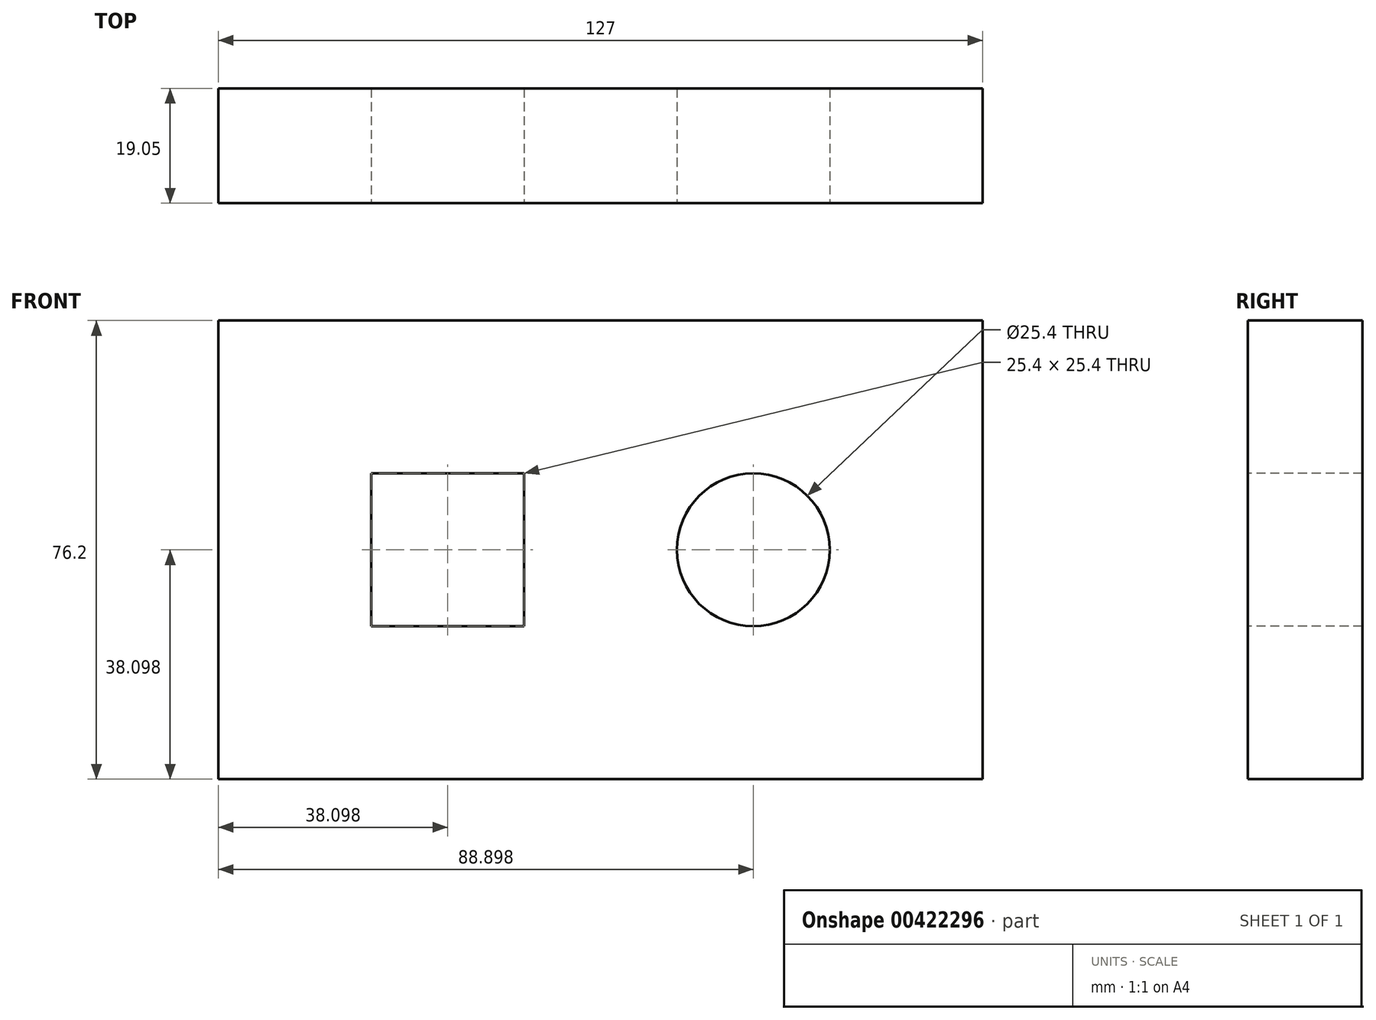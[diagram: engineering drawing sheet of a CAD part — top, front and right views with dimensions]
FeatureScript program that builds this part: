
annotation { "Feature Type Name" : "Feature", "Feature Type Description" : "" }
export const myFeature = defineFeature(function(context is Context, id is Id, definition is map)
    precondition{}
    {
        {
            var Q0;
            Q0=qCreatedBy(makeId("Front.planeOp"),FACE);
            var sketch = newSketch(context, id + "F0", { "sketchPlane" : qUnion([Q0])});
            skLineSegment(sketch, "E0.bottom", {"start": v(-64.45, 53.6) * mm, "end": v(62.55, 53.6) * mm});
            skLineSegment(sketch, "E0.top", {"start": v(-64.45, -22.6) * mm, "end": v(62.55, -22.6) * mm});
            skLineSegment(sketch, "E0.left", {"start": v(-64.45, 53.6) * mm, "end": v(-64.45, -22.6) * mm});
            skLineSegment(sketch, "E0.right", {"start": v(62.55, 53.6) * mm, "end": v(62.55, -22.6) * mm});
            skSolve(sketch);
        }
        {
            var Q0;
            Q0 = qSketchRegion(id + "F0", true);
            extrude(context, id + "F1", {"entities" : qUnion([Q0]), "depth" : 19.05 * mm});
        }
        {
            var Q0;
            Q0=makeQuery(id+"F1.opExtrude","CAP_FACE",FACE,{"disambiguationData":[OSD([sQuery(id+"F0.wireOp",EDGE,"E0.bottom"),sQuery(id+"F0.wireOp",EDGE,"E0.top"),sQuery(id+"F0.wireOp",EDGE,"E0.left"),sQuery(id+"F0.wireOp",EDGE,"E0.right")])],"isStart":false});
            var sketch = newSketch(context, id + "F2", { "sketchPlane" : qUnion([Q0])});
            skLineSegment(sketch, "E1.bottom", {"start": v(-39.05, 28.2) * mm, "end": v(-13.65, 28.2) * mm});
            skLineSegment(sketch, "E1.top", {"start": v(-39.05, 2.8) * mm, "end": v(-13.65, 2.8) * mm});
            skLineSegment(sketch, "E1.left", {"start": v(-39.05, 28.2) * mm, "end": v(-39.05, 2.8) * mm});
            skLineSegment(sketch, "E1.right", {"start": v(-13.65, 28.2) * mm, "end": v(-13.65, 2.8) * mm});
            skCircle(sketch, "E2", {"center": v(24.45, 15.5) * mm, "radius": 12.7 * mm});
            skSolve(sketch);
        }
        {
            var Q0;
            Q0=makeQuery(id+"F2.imprint","IMPRINT",FACE,{"disambiguationData":[TD([[makeQuery(id+"F2.imprint","IMPRINT",EDGE,{"derivedFrom":sQuery(id+"F2.wireOp",EDGE,"E1.bottom")}),-1.0]])]});
            var Q1;
            Q1=makeQuery(id+"F2.imprint","IMPRINT",FACE,{"disambiguationData":[TD([[makeQuery(id+"F2.imprint","IMPRINT",EDGE,{"derivedFrom":sQuery(id+"F2.wireOp",EDGE,"E2")}),1.0]])]});
            extrude(context, id + "F3", {"entities" : qUnion([Q0, Q1]), "operationType" : NewBodyOperationType.REMOVE, "oppositeDirection" : true, "depth" : 25.4 * mm});
        }
    });
